# Revit family: NLRSen_AT_UN_RRBC_Solid_Air
name_source: partatom
category: Air Terminals
revit_build: Autodesk Revit 2017 (Build: 20190508_0315(x64)
units: mm (PartAtom-declared; Revit-internal decimal feet)

## family parameters
Always vertical = Yes
Cut with Voids When Loaded = No
OmniClass Number = 23.75.70.21.27.11
OmniClass Title = Diffusers, Registers, and Grilles
Part Type = Normal
Room Calculation Point = Yes
Round Connector Dimension = Use Diameter
Shared = No
Work Plane-Based = No

## types (4) — shared parameters
Assembly Code = 57.00
Description = Round flanged Swirl return grill, Type RRBC
IfcDescription = Round flanged Swirl return grill, Type RRBC
IfcExportAs = IfcAirterminal
IfcExportType = Diffuser
Lookup_Article_Codes = Grill_Article_Codes
Lookup_Article_Data = RRBC_Article_Data
Lookup_Article_Names = Grill_Article_Names
Lookup_Grill_Factors = Grill_Selection_Factors
Manufacturer = Solid Air Climate Solutions
Model = RRBC
NLRS_C_content_datum_uitgifte = 2019-10-01
NLRS_C_content_provider = Solid Air Climate Solutions
NLRS_C_content_versie = 2.03
NLRS_C_description = Round flanged Swirl return grill, Type RRBC
SACS_AX_Prefix = 820
SACS_Plenum_Material = Sendzimir verzinkt
SACS_Revised_ by = J. Feeke
SACS_Revision_Date = 2019-10-01
SACS_Revision_Number = 2.03
Type Comments = Please make sure flow is set to m3/h!
URL = https://solid-air.nl
zero-valued in all types: Cost

## per-type parameters (varying)
| type | Max Flow | Min Flow | SACS_Base_Index | SACS_Plenum_A | SACS_Plenum_D1 | SACS_Plenum_D2 | SACS_Plenum_D2oval_H | SACS_Plenum_D2oval_W | SACS_Plenum_H | SACS_Plenum_P | SACS_Plenum_Plow | SACS_Plenum_Poval | SACS_Plenum_T |
| 250 | 288 m³/h | 72 m³/h | 1 | 293 mm  [stored 0.961286 ft] | 123 mm  [stored 0.403543 ft] | 123 mm  [stored 0.403543 ft] | 73 mm  [stored 0.239501 ft] | 164 mm  [stored 0.538058 ft] | 110 mm  [stored 0.360892 ft] | 220 mm  [stored 0.721785 ft] | 220 mm  [stored 0.721785 ft] | 200 mm  [stored 0.656168 ft] | 65 mm  [stored 0.213255 ft] |
| 350 | 450 m³/h | 108 m³/h | 2 | 393 mm  [stored 1.28937 ft] | 158 mm | 158 mm | 93 mm  [stored 0.305118 ft] | 208 mm | 125 mm  [stored 0.410105 ft] | 265 mm  [stored 0.869423 ft] | 265 mm  [stored 0.869423 ft] | 230 mm  [stored 0.754593 ft] | 70 mm  [stored 0.229659 ft] |
| 450 | 720 m³/h | 180 m³/h | 3 | 493 mm  [stored 1.61745 ft] | 198 mm  [stored 0.649606 ft] | 198 mm  [stored 0.649606 ft] | 117 mm  [stored 0.383858 ft] | 262 mm  [stored 0.85958 ft] | 140 mm  [stored 0.459318 ft] | 315 mm  [stored 1.03346 ft] | 315 mm  [stored 1.03346 ft] | 250 mm  [stored 0.82021 ft] | 70 mm  [stored 0.229659 ft] |
| 550 | 900 m³/h | 288 m³/h | 4 | 593 mm  [stored 1.94554 ft] | 248 mm  [stored 0.813648 ft] | 248 mm  [stored 0.813648 ft] | 147 mm  [stored 0.482283 ft] | 330 mm  [stored 1.08268 ft] | 160 mm  [stored 0.524934 ft] | 365 mm  [stored 1.19751 ft] | 365 mm  [stored 1.19751 ft] | 285 mm  [stored 0.935039 ft] | 70 mm  [stored 0.229659 ft] |

note: [stored X ft] marks values corroborated as IEEE doubles in the binary element streams (Revit-internal decimal feet)

## geometry (parser evidence)
native form markers: Sweep x20
no freeform markers — native parametric forms only
